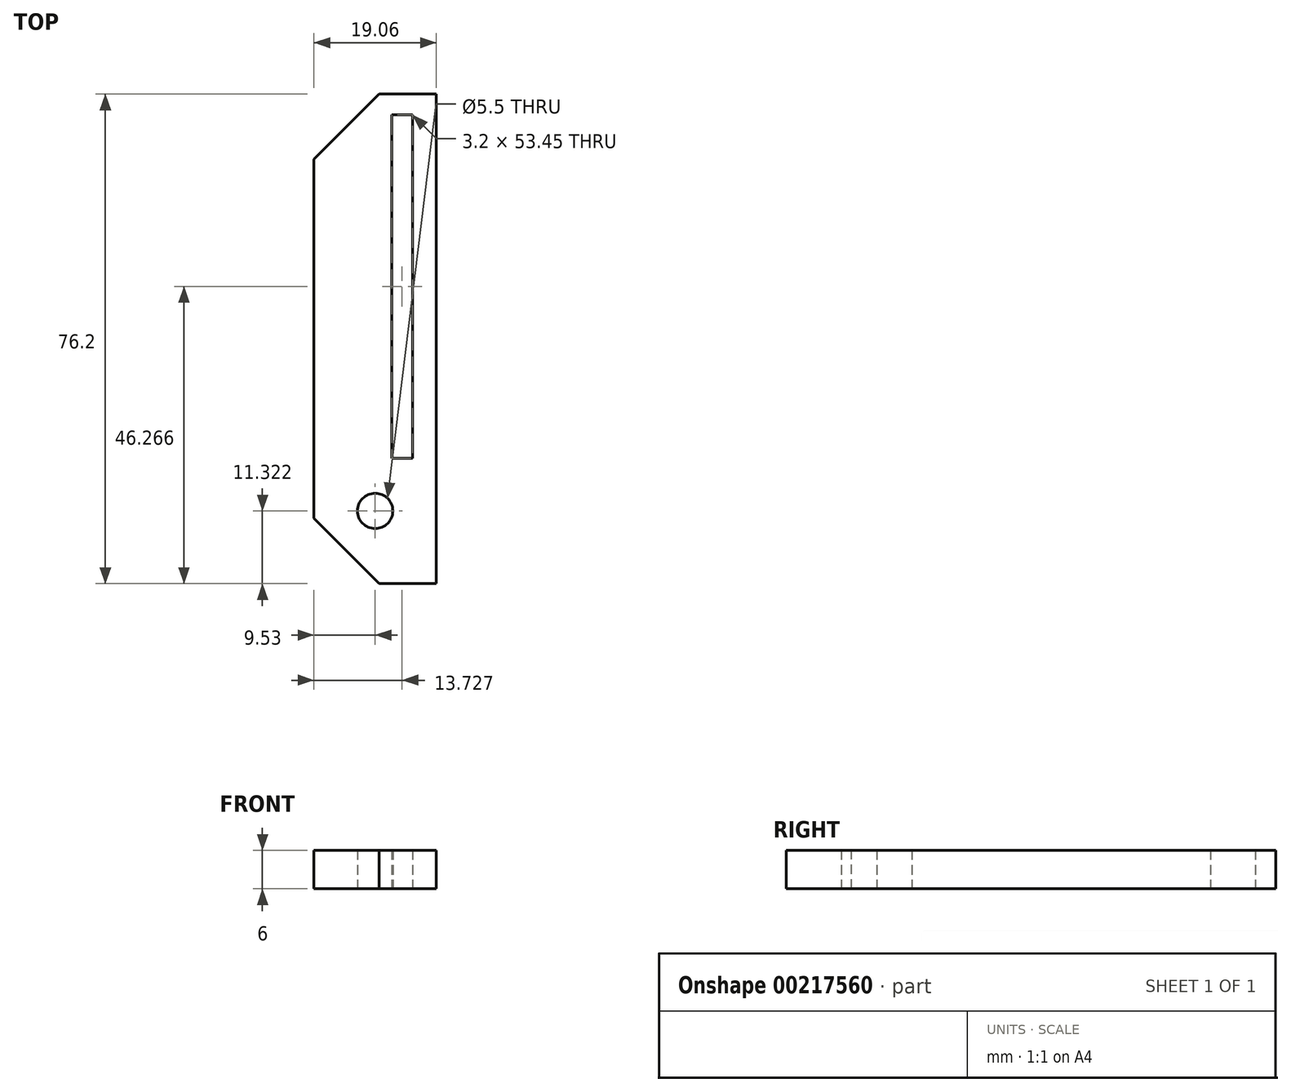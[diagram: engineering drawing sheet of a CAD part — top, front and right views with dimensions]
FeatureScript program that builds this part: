
annotation { "Feature Type Name" : "Feature", "Feature Type Description" : "" }
export const myFeature = defineFeature(function(context is Context, id is Id, definition is map)
    precondition{}
    {
        {
            var Q0;
            Q0=qCreatedBy(makeId("Top.planeOp"),FACE);
            var sketch = newSketch(context, id + "F0", { "sketchPlane" : qUnion([Q0])});
            skLineSegment(sketch, "E0.bottom", {"start": v(9.53, 38.1) * mm, "end": v(-9.52, 38.1) * mm});
            skLineSegment(sketch, "E0.top", {"start": v(9.52, -38.1) * mm, "end": v(-9.53, -38.1) * mm});
            skLineSegment(sketch, "E0.left", {"start": v(9.53, 38.1) * mm, "end": v(9.52, -38.1) * mm});
            skLineSegment(sketch, "E0.right", {"start": v(-9.52, 38.1) * mm, "end": v(-9.53, -38.1) * mm});
            skPoint(sketch, "E0.middle", {"position": v(0, 0) * mm});
            skCircle(sketch, "E1", {"center": v(0, -26.78) * mm, "radius": 2.75 * mm});
            skLineSegment(sketch, "E2.bottom", {"start": v(5.8, 34.9) * mm, "end": v(2.6, 34.9) * mm});
            skLineSegment(sketch, "E3", {"start": v(2.6, 34.9) * mm, "end": v(2.6, -18.56) * mm});
            skLineSegment(sketch, "E4", {"start": v(2.6, -18.56) * mm, "end": v(5.8, -18.56) * mm});
            skLineSegment(sketch, "E5", {"start": v(5.8, -18.56) * mm, "end": v(5.8, 34.9) * mm});
            skSolve(sketch);
        }
        {
            var Q0;
            Q0=makeQuery(id+"F0.imprint","IMPRINT",FACE,{"disambiguationData":[TD([[makeQuery(id+"F0.imprint","IMPRINT",EDGE,{"derivedFrom":sQuery(id+"F0.wireOp",EDGE,"E0.bottom")}),1.0]])]});
            extrude(context, id + "F1", {"entities" : qUnion([Q0]), "depth" : 6 * mm});
        }
        {
            var Q0;
            Q0=makeQuery(id+"F1.opExtrude","SWEPT_EDGE",EDGE,{"disambiguationData":[OSD([sQuery(id+"F0.wireOp",EDGE,"E0.bottom"),sQuery(id+"F0.wireOp",EDGE,"E0.right")])]});
            var Q1;
            Q1=makeQuery(id+"F1.opExtrude","SWEPT_EDGE",EDGE,{"disambiguationData":[OSD([sQuery(id+"F0.wireOp",EDGE,"E0.top"),sQuery(id+"F0.wireOp",EDGE,"E0.right")])]});
            chamfer(context, id + "F2", {"entities" : qUnion([Q0, Q1]), "width" : 10.16 * mm, "tangentPropagation" : true});
        }
    });
